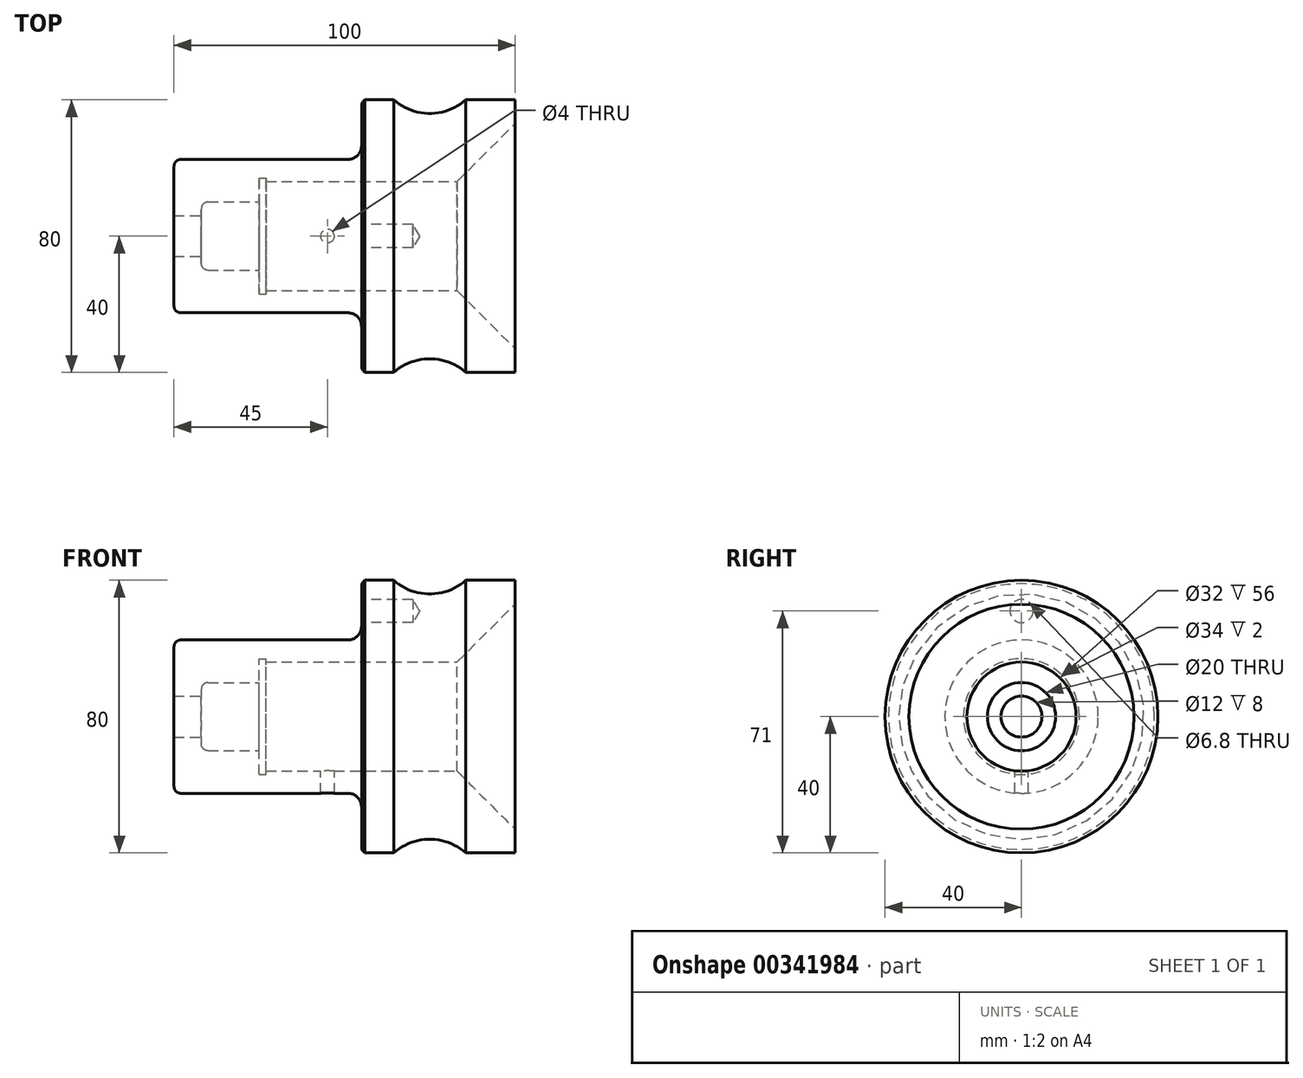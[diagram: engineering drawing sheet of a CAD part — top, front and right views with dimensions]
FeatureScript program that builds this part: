
annotation { "Feature Type Name" : "Feature", "Feature Type Description" : "" }
export const myFeature = defineFeature(function(context is Context, id is Id, definition is map)
    precondition{}
    {
        {
            var Q0;
            Q0=qCreatedBy(makeId("Front.planeOp"),FACE);
            var sketch = newSketch(context, id + "F0", { "sketchPlane" : qUnion([Q0])});
            skLineSegment(sketch, "E0", {"start": v(0, 0) * mm, "end": v(0, 40) * mm});
            skLineSegment(sketch, "E1", {"start": v(0, 40) * mm, "end": v(-45, 40) * mm});
            skLineSegment(sketch, "E2", {"start": v(-45, 40) * mm, "end": v(-45, 22.5) * mm});
            skLineSegment(sketch, "E3", {"start": v(-45, 22.5) * mm, "end": v(-100, 22.5) * mm});
            skLineSegment(sketch, "E4", {"start": v(-100, 22.5) * mm, "end": v(-100, 0) * mm});
            skLineSegment(sketch, "E5", {"start": v(-100, 0) * mm, "end": v(0, 0) * mm});
            skSolve(sketch);
        }
        {
            var Q0;
            Q0=makeQuery(id+"F0.imprint","IMPRINT",FACE,{"disambiguationData":[TD([[makeQuery(id+"F0.imprint","IMPRINT",EDGE,{"derivedFrom":sQuery(id+"F0.wireOp",EDGE,"E0")}),1.0]])]});
            var Q1;
            Q1=sQuery(id+"F0.wireOp",EDGE,"E5");
            revolve(context, id + "F1", {"entities" : qUnion([Q0]), "axis" : qUnion([Q1]), "revolveType" : RevolveType.FULL});
        }
        {
            var Q0;
            Q0=qCreatedBy(makeId("Front.planeOp"),FACE);
            var sketch = newSketch(context, id + "F2", { "sketchPlane" : qUnion([Q0])});
            skLineSegment(sketch, "E6", {"start": v(0, 0) * mm, "end": v(0, 33) * mm});
            skLineSegment(sketch, "E7", {"start": v(0, 33) * mm, "end": v(-17, 16) * mm});
            skLineSegment(sketch, "E8", {"start": v(-17, 16) * mm, "end": v(-73, 16) * mm});
            skLineSegment(sketch, "E9", {"start": v(-73, 16) * mm, "end": v(-73, 17) * mm});
            skLineSegment(sketch, "E10", {"start": v(-73, 17) * mm, "end": v(-75, 17) * mm});
            skLineSegment(sketch, "E11", {"start": v(-75, 17) * mm, "end": v(-75, 10) * mm});
            skLineSegment(sketch, "E12", {"start": v(-75, 10) * mm, "end": v(-92, 10) * mm});
            skLineSegment(sketch, "E13", {"start": v(-92, 10) * mm, "end": v(-92, 6) * mm});
            skLineSegment(sketch, "E14", {"start": v(-92, 6) * mm, "end": v(-100, 6) * mm});
            skLineSegment(sketch, "E15", {"start": v(-100, 6) * mm, "end": v(-100, 0) * mm});
            skLineSegment(sketch, "E16", {"start": v(-100, 0) * mm, "end": v(0, 0) * mm});
            skSolve(sketch);
        }
        {
            var Q0;
            Q0=qSketchRegion(id+"F2",true);
            var Q1;
            Q1=sQuery(id+"F2.wireOp",EDGE,"E16");
            revolve(context, id + "F3", {"operationType" : NewBodyOperationType.REMOVE, "entities" : qUnion([Q0]), "axis" : qUnion([Q1]), "revolveType" : RevolveType.FULL, "oppositeDirection" : true});
        }
        {
            var Q0;
            Q0=qCreatedBy(makeId("Front.planeOp"),FACE);
            var sketch = newSketch(context, id + "F4", { "sketchPlane" : qUnion([Q0])});
            skCircle(sketch, "E17", {"center": v(-25, 52) * mm, "radius": 16 * mm});
            skSolve(sketch);
        }
        {
            var Q0;
            Q0=makeQuery(id+"F4.imprint","IMPRINT",FACE,{"disambiguationData":[TD([[makeQuery(id+"F4.imprint","IMPRINT",EDGE,{"derivedFrom":sQuery(id+"F4.wireOp",EDGE,"E17")}),1.0]])]});
            var Q1;
            Q1=sQuery(id+"F0.wireOp",EDGE,"E5");
            revolve(context, id + "F5", {"operationType" : NewBodyOperationType.REMOVE, "entities" : qUnion([Q0]), "axis" : qUnion([Q1]), "revolveType" : RevolveType.FULL, "oppositeDirection" : true});
        }
        {
            var Q0;
            Q0=qCreatedBy(makeId("Top.planeOp"),FACE);
            var sketch = newSketch(context, id + "F6", { "sketchPlane" : qUnion([Q0])});
            skCircle(sketch, "E18", {"center": v(-55, 0) * mm, "radius": 2 * mm});
            skSolve(sketch);
        }
        {
            var Q0;
            Q0=qSketchRegion(id+"F6",true);
            extrude(context, id + "F7", {"entities" : qUnion([Q0]), "operationType" : NewBodyOperationType.REMOVE, "endBound" : BoundingType.THROUGH_ALL, "oppositeDirection" : true, "depth" : 25 * mm});
        }
        {
            var Q0;
            Q0=makeQuery(id+"F1.opRevolve","SWEPT_FACE",FACE,{"disambiguationData":[OSD([sQuery(id+"F0.wireOp",EDGE,"E2")])]});
            var sketch = newSketch(context, id + "F8", { "sketchPlane" : qUnion([Q0])});
            skPoint(sketch, "E19", {"position": v(0, 31) * mm});
            skSolve(sketch);
        }
        {
            var Q0;
            Q0=sQuery(id+"F8.wireOp",VERTEX,"E19");
            var Q1;
            Q1=makeQuery(id+"F1.opRevolve","SWEPT_BODY",BODY,{"disambiguationData":[OSD([sQuery(id+"F0.wireOp",EDGE,"E0"),sQuery(id+"F0.wireOp",EDGE,"E1"),sQuery(id+"F0.wireOp",EDGE,"E2"),sQuery(id+"F0.wireOp",EDGE,"E3"),sQuery(id+"F0.wireOp",EDGE,"E4"),sQuery(id+"F0.wireOp",EDGE,"E5")])]});
            hole(context, id + "F9", {"style" : HoleStyle.SIMPLE, "endStyle" : HoleEndStyle.BLIND, "standardTappedOrClearance" : lookupTablePath({ "standard" : "ISO", "engagement" : "75%", "pitch" : "1.25 mm", "size" : "M8", "type" : "Tapped" }), "standardBlindInLast" : lookupTablePath({ "standard" : "ISO", "engagement" : "75%", "pitch" : "1.25 mm", "size" : "M8", "type" : "Tapped" }), "holeDiameter" : 6.8 * mm, "showTappedDepth" : true, "holeDepth" : 15 * mm, "tappedDepth" : 10 * mm, "tapClearance" : 4, "locations" : qUnion([Q0]), "scope" : qUnion([Q1]), "majorDiameter" : 8 * mm});
        }
        {
            var Q0;
            Q0=makeQuery(id+"F1.opRevolve","SWEPT_EDGE",EDGE,{"disambiguationData":[OSD([sQuery(id+"F0.wireOp",EDGE,"E1"),sQuery(id+"F0.wireOp",EDGE,"E2")])]});
            chamfer(context, id + "F10", {"entities" : qUnion([Q0]), "width" : 1 * mm, "tangentPropagation" : true});
        }
        {
            var Q0;
            Q0=makeQuery(id+"F1.opRevolve","SWEPT_EDGE",EDGE,{"disambiguationData":[OSD([sQuery(id+"F0.wireOp",EDGE,"E3"),sQuery(id+"F0.wireOp",EDGE,"E4")])]});
            var Q1;
            Q1=makeQuery(id+"F3.boolean.opBoolean","COPY",EDGE,{"derivedFrom":makeQuery(id+"F3.opRevolve","SWEPT_EDGE",EDGE,{"disambiguationData":[OSD([sQuery(id+"F2.wireOp",EDGE,"E12"),sQuery(id+"F2.wireOp",EDGE,"E13")])]})});
            fillet(context, id + "F11", {"entities" : qUnion([Q0, Q1]), "radius" : 2 * mm, "tangentPropagation" : true, "allowEdgeOverflow" : false});
        }
        {
            var Q0;
            Q0=makeQuery(id+"F1.opRevolve","SWEPT_EDGE",EDGE,{"disambiguationData":[OSD([sQuery(id+"F0.wireOp",EDGE,"E2"),sQuery(id+"F0.wireOp",EDGE,"E3")])]});
            fillet(context, id + "F12", {"entities" : qUnion([Q0]), "radius" : 4 * mm, "tangentPropagation" : true, "allowEdgeOverflow" : false});
        }
    });
